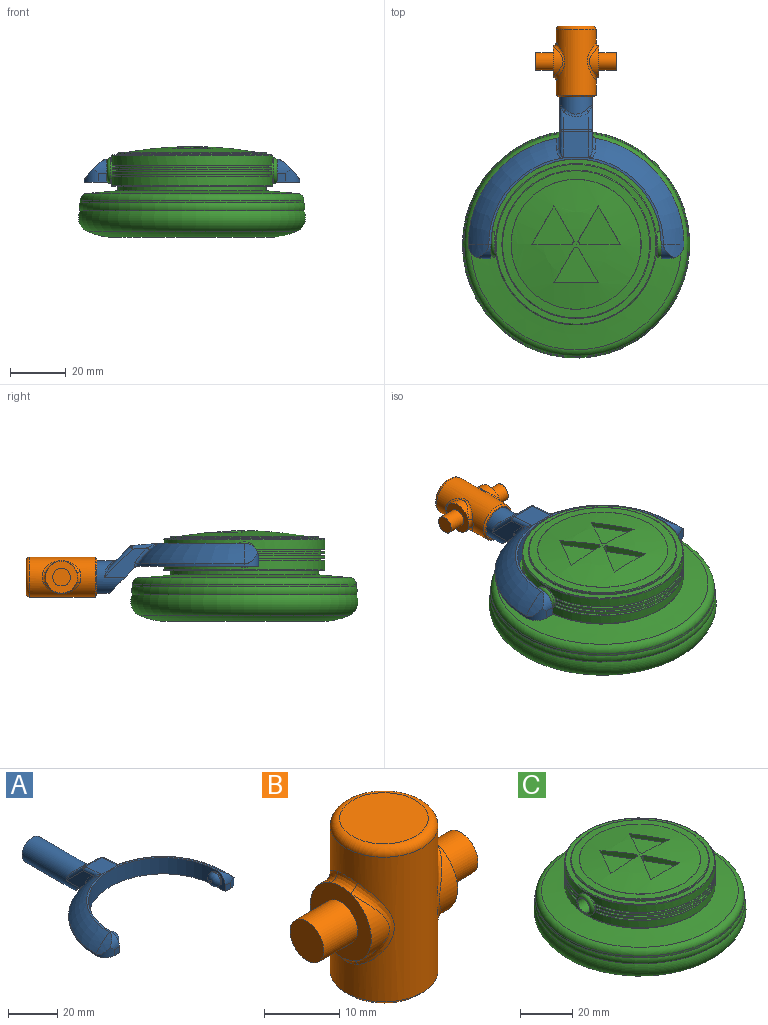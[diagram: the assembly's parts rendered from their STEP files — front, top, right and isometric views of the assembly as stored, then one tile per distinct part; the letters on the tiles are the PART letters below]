
ASSEMBLY  parts=3 mates=2
PART A: 48 faces, bbox 77.3x80.8x18.2 mm
  f0: plane 11.99x9.83mm, normal (0,-0.71,-0.71), area 141.5mm2, adj f1,f2,f9,f30,f43,f46
  f1: plane 15.39x10.49mm, normal (-1,0,0), area 63.5mm2, adj f0,f30,f32,f36,f46,f47
  f2: plane 15.39x10.49mm, normal (1,0,0), area 63.5mm2, adj f0,f30,f34,f39,f43,f44
  f3: plane 9.14x6.37mm, normal (0,0.71,0.71), area 67.6mm2, adj f35,f36,f39,f40
  f4: cylinder r=38.61mm len=37.99mm, axis (0,0,-1), area 42.6mm2, adj f6,f9,f17,f46,f47
  f5: torus R=19.3mm, axis (0,0,-1), area 507.8mm2, adj f10,f11,f12,f29,f42,f44
  f6: torus R=19.3mm, axis (0,0,-1), area 507.8mm2, adj f4,f11,f15,f28,f45,f47
  f7: cylinder r=30.48mm len=60.96mm, axis (0,0,-1), area 746.6mm2, adj f8,f9,f11,f14,f21,f24
  f8: plane 8.13x5.08mm, normal (-1,0,0), area 19.9mm2, adj f7,f9,f13,f19,f24
  f9: plane 77.22x43.73mm, normal (0,0,-1), area 956.2mm2, adj f0,f4,f7,f8,f10,f13,f14,f16
  f10: cylinder r=38.61mm len=37.99mm, axis (0,0,-1), area 42.6mm2, adj f5,f9,f20,f43,f44
  f11: plane 62.55x30.95mm, normal (0,0,1), area 75mm2, adj f5,f6,f7,f18,f19,f27
  f12: cylinder r=22.71mm len=7.33mm, axis (0,1,0), area 24.8mm2, adj f5,f19,f20
  f13: plane 3.05x3.05mm, normal (0,-1,0), area 9.3mm2, adj f8,f9,f19,f20
  f14: plane 8.13x5.08mm, normal (1,0,0), area 19.9mm2, adj f7,f9,f16,f18,f21
  f15: cylinder r=22.71mm len=7.33mm, axis (0,1,0), area 24.8mm2, adj f6,f17,f18
  f16: plane 3.05x3.05mm, normal (0,-1,0), area 9.3mm2, adj f9,f14,f17,f18
  f17: cylinder r=5.08mm len=5.08mm, axis (0,0,-1), area 21.9mm2, adj f4,f9,f15,f16,f18
  f18: cylinder r=5.08mm len=5.08mm, axis (-1,0,0), area 21.9mm2, adj f11,f14,f15,f16,f17
  f19: cylinder r=5.08mm len=5.08mm, axis (-1,0,0), area 21.9mm2, adj f8,f11,f12,f13,f20
  f20: cylinder r=5.08mm len=5.08mm, axis (0,0,-1), area 21.9mm2, adj f9,f10,f12,f13,f19
  f21: cylinder r=3.17mm len=6.35mm, axis (-1,0,0), area 12.7mm2, adj f7,f14,f23
  f22: plane 1.27x1.27mm, normal (1,0,0), area 1.3mm2, adj f23
  f23: torus R=0.64mm, axis (1,0,0), area 56.5mm2, adj f21,f22
  f24: cylinder r=3.17mm len=6.35mm, axis (1,0,0), area 12.7mm2, adj f7,f8,f26
  f25: plane 1.27x1.27mm, normal (-1,0,0), area 1.3mm2, adj f26
  f26: torus R=0.64mm, axis (-1,0,0), area 56.5mm2, adj f24,f25
  f27: plane 9.86x9.36mm, normal (0,0.09,1), area 85.6mm2, adj f11,f28,f29,f32,f34,f35,f42,f45
  f28: plane 1.04x0.17mm, normal (0,-1,0), area 0mm2, adj f6,f27,f45
  f29: plane 1.04x0.17mm, normal (0,-1,0), area 0mm2, adj f5,f27,f42
  f30: cylinder r=5.84mm len=33.01mm, axis (0,-1,0), area 1029.7mm2, adj f0,f1,f2,f31,f38,f40,f41
  f31: plane 11.68x11.68mm, normal (0,1,0), area 107.2mm2, adj f30
  f32: cylinder r=1.27mm len=9.13mm, axis (0,-1,0.09), area 14.4mm2, adj f1,f27,f33,f45
  f33: sphere r=1.27mm, area 1.5mm2, adj f32,f35,f36
  f34: cylinder r=1.27mm len=9.13mm, axis (0,1,-0.09), area 14.4mm2, adj f2,f27,f37,f42
  f35: cylinder r=1.27mm len=9.14mm, axis (-1,0,0), area 8.1mm2, adj f3,f27,f33,f37
  f36: cylinder r=1.27mm len=10.91mm, axis (0,-0.71,0.71), area 23.1mm2, adj f1,f3,f33,f38
  f37: sphere r=1.27mm, area 1.5mm2, adj f34,f35,f39
  f38: bspline ~4.55x2.75mm, area 2.3mm2, adj f30,f36,f40
  f39: cylinder r=1.27mm len=10.91mm, axis (0,0.71,-0.71), area 23.1mm2, adj f2,f3,f37,f41
  f40: bspline ~9.14x2.56mm, area 10.7mm2, adj f3,f30,f38,f41
  f41: bspline ~5.23x3.53mm, area 2.3mm2, adj f30,f39,f40
  f42: bspline ~4.62x3.14mm, area 5.2mm2, adj f5,f27,f29,f34,f44
  f43: cylinder r=1.27mm len=1.74mm, axis (0,0,-1), area 1.9mm2, adj f0,f2,f9,f10,f44
  f44: bspline ~8.6x7.86mm, area 11.9mm2, adj f2,f5,f10,f42,f43
  f45: bspline ~4.62x3.14mm, area 5.2mm2, adj f6,f27,f28,f32,f47
  f46: cylinder r=1.27mm len=1.74mm, axis (0,0,-1), area 1.9mm2, adj f0,f1,f4,f9,f47
  f47: bspline ~8.6x7.86mm, area 11.9mm2, adj f1,f4,f6,f45,f46
PART B: 25 faces, bbox 28.9x15.5x25.4 mm
  f0: cylinder r=5.71mm len=10.81mm, axis (-1,0,0), area 26.2mm2, adj f5,f15
  f1: cylinder r=5.71mm len=10.81mm, axis (-1,0,0), area 26.2mm2, adj f8,f11
  f2: cylinder r=7.14mm len=23.5mm, axis (0,0,-1), area 763.2mm2, adj f9,f10,f11,f12,f13,f14,f15,f16
  f3: plane 11.75x11.75mm, normal (0,0,1), area 108.4mm2, adj f17
  f4: plane 13.02x13.02mm, normal (0,0,-1), area 16.3mm2, adj f22,f24
  f5: plane 11.46x11.46mm, normal (1,0,0), area 70.9mm2, adj f0,f6,f13,f16,f18
  f6: cylinder r=5.71mm len=10.81mm, axis (-1,0,0), area 26.2mm2, adj f5,f14
  f7: cylinder r=5.71mm len=10.81mm, axis (-1,0,0), area 26.2mm2, adj f8,f10
  f8: plane 11.46x11.46mm, normal (-1,0,0), area 70.9mm2, adj f1,f7,f9,f12,f20
  f9: bspline ~4.64x1.73mm, area 6.5mm2, adj f2,f8,f10,f11
  f10: bspline ~13.62x4.91mm, area 20.7mm2, adj f2,f7,f9,f12
  f11: bspline ~13.6x4.87mm, area 20.7mm2, adj f1,f2,f9,f12
  f12: bspline ~4.64x1.73mm, area 6.5mm2, adj f2,f8,f10,f11
  f13: bspline ~4.64x1.73mm, area 6.5mm2, adj f2,f5,f14,f15
  f14: bspline ~13.62x4.91mm, area 20.7mm2, adj f2,f6,f13,f16
  f15: bspline ~13.6x4.87mm, area 20.7mm2, adj f0,f2,f13,f16
  f16: bspline ~4.64x1.73mm, area 6.5mm2, adj f2,f5,f14,f15
  f17: torus R=5.87mm, axis (0,0,1), area 83.8mm2, adj f2,f3
  f18: cylinder r=3.17mm len=6.35mm, axis (-1,0,0), area 126.7mm2, adj f5,f19
  f19: plane 6.35x6.35mm, normal (1,0,0), area 31.7mm2, adj f18
  f20: cylinder r=3.17mm len=6.35mm, axis (1,0,0), area 126.7mm2, adj f8,f21
  f21: plane 6.35x6.35mm, normal (-1,0,0), area 31.7mm2, adj f20
  f22: cylinder r=6.1mm len=22.86mm, axis (0,0,-1), area 875.6mm2, adj f4,f23
  f23: plane 12.19x12.19mm, normal (0,0,-1), area 116.7mm2, adj f22
  f24: cone r=7.14mm half-angle=45deg, axis (0,0,1), area 38.5mm2, adj f2,f4
PART C: 64 faces, bbox 96.2x96.2x32.5 mm
  f0: sphere r=135.39mm, area 1385.3mm2, adj f48,f49,f50,f51,f52,f54,f55,f56
  f1: cylinder r=28.87mm len=57.73mm, axis (0,0,-1), area 595.8mm2, adj f2,f3,f39,f40,f45
  f2: plane 57.13x24.71mm, normal (0,0,1), area 102mm2, adj f1,f7,f39,f40
  f3: plane 57.13x24.71mm, normal (0,0,1), area 102mm2, adj f1,f6,f39,f40
  f4: plane 57.06x24.48mm, normal (0,0,-1), area 101.4mm2, adj f7,f8,f39,f40
  f5: plane 57.06x24.48mm, normal (0,0,-1), area 101.4mm2, adj f6,f9,f39,f40
  f6: cylinder r=27.6mm len=54.56mm, axis (0,0,1), area 49.6mm2, adj f3,f5,f39,f40
  f7: cylinder r=27.6mm len=54.56mm, axis (0,0,1), area 49.6mm2, adj f2,f4,f39,f40
  f8: cylinder r=28.87mm len=57.06mm, axis (0,0,-1), area 77.8mm2, adj f4,f14,f39,f40
  f9: cylinder r=28.87mm len=57.06mm, axis (0,0,-1), area 77.8mm2, adj f5,f15,f39,f40
  f10: plane 57.01x24.31mm, normal (0,0,-1), area 101mm2, adj f13,f16,f39,f40
  f11: plane 57.01x24.31mm, normal (0,0,-1), area 101mm2, adj f12,f17,f39,f40
  f12: cylinder r=27.6mm len=54.44mm, axis (0,0,1), area 49.2mm2, adj f11,f15,f39,f40
  f13: cylinder r=27.6mm len=54.44mm, axis (0,0,1), area 49.2mm2, adj f10,f14,f39,f40
  f14: plane 57.01x24.31mm, normal (0,0,1), area 101mm2, adj f8,f13,f39,f40
  f15: plane 57.01x24.31mm, normal (0,0,1), area 101mm2, adj f9,f12,f39,f40
  f16: cylinder r=28.87mm len=57.06mm, axis (0,0,-1), area 77.8mm2, adj f10,f22,f39,f40
  f17: cylinder r=28.87mm len=57.06mm, axis (0,0,-1), area 77.8mm2, adj f11,f23,f39,f40
  f18: plane 57.13x24.71mm, normal (0,0,-1), area 102mm2, adj f21,f24,f39,f40
  f19: plane 57.13x24.71mm, normal (0,0,-1), area 102mm2, adj f20,f24,f39,f40
  f20: cylinder r=27.6mm len=54.56mm, axis (0,0,1), area 49.6mm2, adj f19,f23,f39,f40
  f21: cylinder r=27.6mm len=54.56mm, axis (0,0,1), area 49.6mm2, adj f18,f22,f39,f40
  f22: plane 57.06x24.48mm, normal (0,0,1), area 101.4mm2, adj f16,f21,f39,f40
  f23: plane 57.06x24.48mm, normal (0,0,1), area 101.4mm2, adj f17,f20,f39,f40
  f24: cylinder r=28.87mm len=57.73mm, axis (0,0,-1), area 595.8mm2, adj f18,f19,f39,f40,f46
  f25: plane 39.33x39.33mm, normal (0,0,-1), area 1214.6mm2, adj f26
  f26: torus R=20.12mm, axis (0,0,-1), area 1429.3mm2, adj f25,f27
  f27: torus R=27.74mm, axis (0,0,-1), area 3542.1mm2, adj f26,f28
  f28: torus R=35.36mm, axis (0,0,-1), area 2180.1mm2, adj f27,f29
  f29: torus R=37.35mm, axis (0,0,-1), area 734.6mm2, adj f28,f30
  f30: cylinder r=40.06mm len=80.11mm, axis (0,0,-1), area 213.3mm2, adj f29,f34
  f31: cone r=26.58mm half-angle=85deg, axis (0,0,-1), area 2262.8mm2, adj f32,f34
  f32: cylinder r=26.58mm len=53.16mm, axis (0,0,-1), area 265.1mm2, adj f31,f33
  f33: plane 57.23x57.23mm, normal (0,0,-1), area 352.3mm2, adj f32,f45
  f34: torus R=37.52mm, axis (0,0,1), area 928.6mm2, adj f30,f31
  f35: cone r=26.58mm half-angle=87deg, axis (0,0,-1), area 477.5mm2, adj f47,f48
  f36: cylinder r=26.58mm len=53.16mm, axis (0,0,-1), area 92.3mm2, adj f37,f47
  f37: plane 57.23x57.23mm, normal (0,0,1), area 352.3mm2, adj f36,f46
  f38: plane 6.6x6.6mm, normal (1,0,0), area 2.6mm2, adj f43,f44
  f39: cylinder r=4.57mm len=9.14mm, axis (-1,0,0), area 20.2mm2, adj f1,f2,f3,f4,f5,f6,f7,f8
  f40: cylinder r=4.57mm len=9.14mm, axis (-1,0,0), area 20.2mm2, adj f1,f2,f3,f4,f5,f6,f7,f8
  f41: plane 6.6x6.6mm, normal (-1,0,0), area 2.6mm2, adj f42,f44
  f42: torus R=3.3mm, axis (1,0,0), area 51.5mm2, adj f40,f41
  f43: torus R=3.3mm, axis (1,0,0), area 51.5mm2, adj f38,f39
  f44: cylinder r=3.17mm len=60.96mm, axis (1,0,0), area 1216.1mm2, adj f38,f41
  f45: torus R=28.61mm, axis (0,0,1), area 72.1mm2, adj f1,f33
  f46: torus R=28.61mm, axis (0,0,-1), area 72.1mm2, adj f24,f37
  f47: torus R=26.33mm, axis (0,0,1), area 64.2mm2, adj f35,f36
  f48: torus R=23.29mm, axis (0,0,1), area 4.5mm2, adj f0,f35
  f49: cylinder r=1.27mm len=2.53mm, axis (0,0,1), area 3.4mm2, adj f0,f50,f52,f53
  f50: plane 14.61x2.53mm, normal (0,1,0), area 32.2mm2, adj f0,f49,f51,f53
  f51: plane 13.75x7.94mm, normal (-0.87,-0.5,0), area 28mm2, adj f0,f50,f52,f53
  f52: plane 12.65x7.3mm, normal (0.87,-0.5,0), area 32.2mm2, adj f0,f49,f51,f53
  f53: plane 15.24x13.75mm, normal (0,0,1), area 108.3mm2, adj f49,f50,f51,f52
  f54: cylinder r=1.27mm len=2.53mm, axis (0,0,1), area 3.4mm2, adj f0,f55,f57,f58
  f55: plane 12.65x7.3mm, normal (0.87,-0.5,0), area 32.2mm2, adj f0,f54,f56,f58
  f56: plane 15.88x1.84mm, normal (0,1,0), area 28mm2, adj f0,f55,f57,f58
  f57: plane 12.65x7.3mm, normal (-0.87,-0.5,0), area 32.2mm2, adj f0,f54,f56,f58
  f58: plane 15.88x12.65mm, normal (0,0,1), area 108.3mm2, adj f54,f55,f56,f57
  f59: plane 13.75x7.94mm, normal (0.87,-0.5,0), area 28mm2, adj f0,f60,f62,f63
  f60: plane 14.61x2.53mm, normal (0,1,0), area 32.2mm2, adj f0,f59,f61,f63
  f61: cylinder r=1.27mm len=2.53mm, axis (0,0,1), area 3.4mm2, adj f0,f60,f62,f63
  f62: plane 12.65x7.3mm, normal (-0.87,-0.5,0), area 32.2mm2, adj f0,f59,f61,f63
  f63: plane 15.24x13.75mm, normal (0,0,1), area 108.3mm2, adj f59,f60,f61,f62
PLACE A t=(32.34,27.52,20.85)mm
PLACE B rot(axis=(-1,0,0),90deg) t=(32.34,80.3,16.88)mm
PLACE C t=(32.34,27.52,33.52)mm
MATE revolute A.f24 <-> C.f39  axis (-1,0,0) through (62.82,27.52,24.92)mm
MATE revolute B.f2 <-> A.f30  axis (0,-1,0) through (32.34,103.16,16.88)mm
